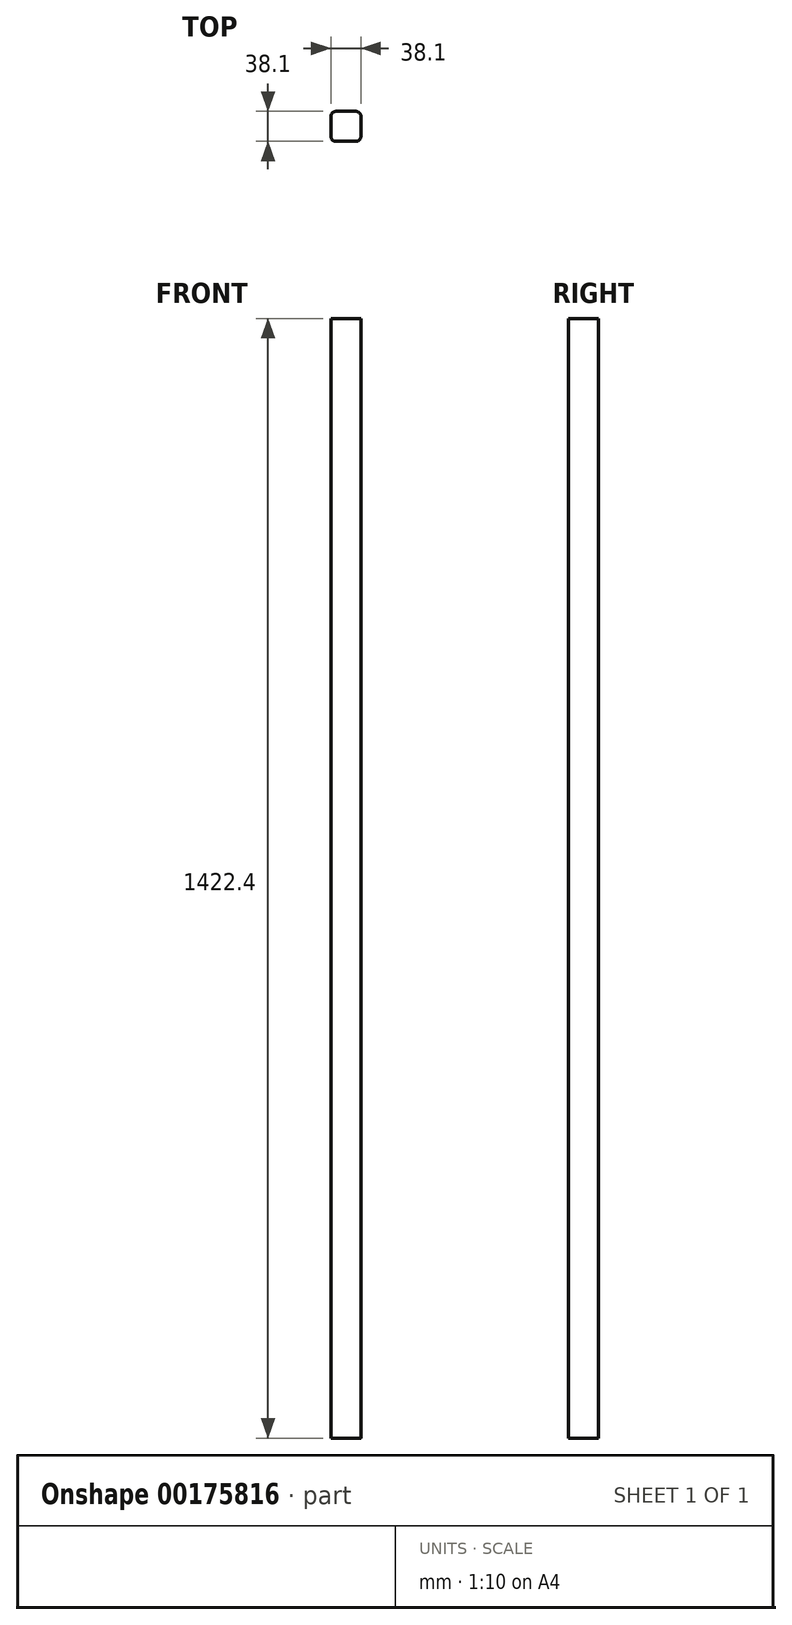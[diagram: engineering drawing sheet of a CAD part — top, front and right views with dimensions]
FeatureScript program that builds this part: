
annotation { "Feature Type Name" : "Feature", "Feature Type Description" : "" }
export const myFeature = defineFeature(function(context is Context, id is Id, definition is map)
    precondition{}
    {
        {
            var Q0;
            Q0=qCreatedBy(makeId("Top.planeOp"),FACE);
            var sketch = newSketch(context, id + "F0", { "sketchPlane" : qUnion([Q0])});
            skLineSegment(sketch, "E0.bottom", {"start": v(12.7, 19.05) * mm, "end": v(-12.7, 19.05) * mm});
            skLineSegment(sketch, "E0.top", {"start": v(12.7, -19.05) * mm, "end": v(-12.7, -19.05) * mm});
            skLineSegment(sketch, "E0.left", {"start": v(19.05, 12.7) * mm, "end": v(19.05, -12.7) * mm});
            skLineSegment(sketch, "E0.right", {"start": v(-19.05, 12.7) * mm, "end": v(-19.05, -12.7) * mm});
            skPoint(sketch, "E0.middle", {"position": v(0, 0) * mm});
            skPoint(sketch, "E1.visualSharp", {"position": v(-19.05, 19.05) * mm});
            skArc(sketch, "E1.filletArc", {"start": v(-12.7, 19.05) * mm, "mid": v(-17.2, 17.2) * mm, "end": v(-19.05, 12.7) * mm});
            skPoint(sketch, "E2.visualSharp", {"position": v(19.05, 19.05) * mm});
            skArc(sketch, "E2.filletArc", {"start": v(19.05, 12.7) * mm, "mid": v(17.2, 17.2) * mm, "end": v(12.7, 19.05) * mm});
            skPoint(sketch, "E3.visualSharp", {"position": v(19.05, -19.05) * mm});
            skArc(sketch, "E3.filletArc", {"start": v(12.7, -19.05) * mm, "mid": v(17.2, -17.2) * mm, "end": v(19.05, -12.7) * mm});
            skPoint(sketch, "E4.visualSharp", {"position": v(-19.05, -19.05) * mm});
            skArc(sketch, "E4.filletArc", {"start": v(-19.05, -12.7) * mm, "mid": v(-17.2, -17.2) * mm, "end": v(-12.7, -19.05) * mm});
            skSolve(sketch);
        }
        {
            var Q0;
            Q0=qSketchRegion(id+"F0",true);
            extrude(context, id + "F1", {"entities" : qUnion([Q0]), "depth" : 1422.4 * mm, "offsetDistance" : 25.4 * mm});
        }
    });
